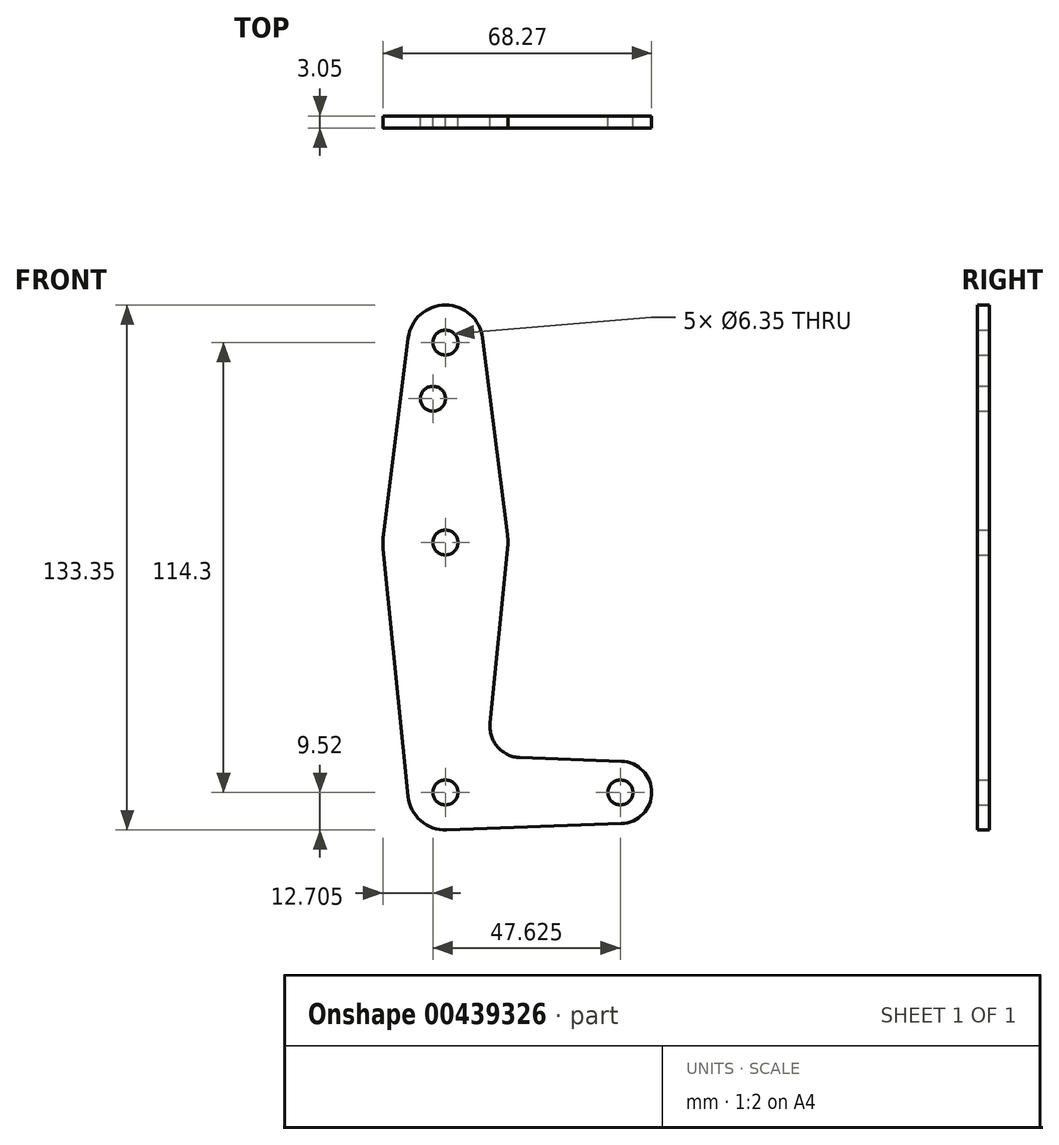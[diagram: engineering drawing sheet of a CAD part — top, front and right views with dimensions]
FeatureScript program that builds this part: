
annotation { "Feature Type Name" : "Feature", "Feature Type Description" : "" }
export const myFeature = defineFeature(function(context is Context, id is Id, definition is map)
    precondition{}
    {
        {
            var Q0;
            Q0=qCreatedBy(makeId("Front.planeOp"),FACE);
            var sketch = newSketch(context, id + "F0", { "sketchPlane" : qUnion([Q0])});
            skLineSegment(sketch, "E0", {"start": v(0, 114.3) * mm, "end": v(0, 0) * mm, "construction": true});
            skLineSegment(sketch, "E1", {"start": v(0, 0) * mm, "end": v(44.45, 0) * mm, "construction": true});
            skCircle(sketch, "E2", {"center": v(0, 114.3) * mm, "radius": 9.53 * mm});
            skCircle(sketch, "E3", {"center": v(0, 63.5) * mm, "radius": 15.88 * mm});
            skCircle(sketch, "E4", {"center": v(0, 0) * mm, "radius": 9.53 * mm});
            skCircle(sketch, "E5", {"center": v(44.45, 0) * mm, "radius": 7.94 * mm});
            skLineSegment(sketch, "E6", {"start": v(-9.45, 115.5) * mm, "end": v(-15.75, 65.48) * mm});
            skLineSegment(sketch, "E7", {"start": v(9.45, 115.5) * mm, "end": v(15.75, 65.48) * mm});
            skLineSegment(sketch, "E8", {"start": v(-15.8, 61.91) * mm, "end": v(-9.48, -0.95) * mm});
            skLineSegment(sketch, "E9", {"start": v(15.8, 61.91) * mm, "end": v(11.34, 17.6) * mm});
            skLineSegment(sketch, "E10", {"start": v(0.34, -9.52) * mm, "end": v(44.73, -7.93) * mm});
            skLineSegment(sketch, "E11", {"start": v(18.97, 8.85) * mm, "end": v(44.73, 7.93) * mm});
            skCircle(sketch, "E12", {"center": v(0, 114.3) * mm, "radius": 3.18 * mm});
            skCircle(sketch, "E13", {"center": v(0, 63.5) * mm, "radius": 3.18 * mm});
            skCircle(sketch, "E14", {"center": v(0, 0) * mm, "radius": 3.18 * mm});
            skCircle(sketch, "E15", {"center": v(44.45, 0) * mm, "radius": 3.18 * mm});
            skCircle(sketch, "E16", {"center": v(-3.17, 100.03) * mm, "radius": 3.18 * mm});
            skArc(sketch, "E17.filletArc", {"start": v(11.34, 17.6) * mm, "mid": v(13.26, 11.57) * mm, "end": v(18.97, 8.85) * mm});
            skSolve(sketch);
        }
        {
            var Q0;
            Q0 = qSketchRegion(id + "F0", true);
            extrude(context, id + "F1", {"entities" : qUnion([Q0]), "depth" : 3.05 * mm});
        }
    });
